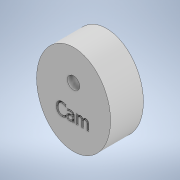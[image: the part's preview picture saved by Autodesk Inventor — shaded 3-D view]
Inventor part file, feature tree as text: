
AUTODESK INVENTOR PART (.ipt)
format: ipt  version: 2021 (Build 250183000, 183)  size: 234,496 bytes
history: native  units: mm
features: sketch x2, extrude x1, emboss x1
ambient origin geometry x8: Origin, YZ Plane, XZ Plane, XY Plane, X Axis, Y Axis, Z Axis, Center Point
bodies: Solid1 (feature_tree)
feature tree (4):
  extrude  "Extrusion1"  Depth=11.0mm
  emboss  "Emboss1"
  sketch  "Sketch1"  dims[d0=9.0mm d1=11.0mm]
  sketch  "Sketch2"  dims[d2=3.0mm d3=3.5mm d4=8.0mm d5=0.0mm d6=1.0mm d7=0.0mm]
